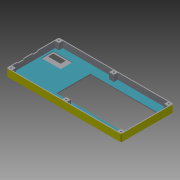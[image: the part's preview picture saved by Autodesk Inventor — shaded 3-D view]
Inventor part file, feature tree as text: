
AUTODESK INVENTOR PART (.ipt)
format: ipt  version: 2015 (Build 190159000, 159)  size: 203,776 bytes
history: native  units: mm
features: extrude x7, sketch x7, other x1, fillet x1
ambient origin geometry x8: Origin, YZ Plane, XZ Plane, XY Plane, X Axis, Y Axis, Z Axis, Center Point
bodies: Body1 (feature_tree)
feature tree (16):
  other  "ソリッド1"
  extrude  "天板"  Depth=240.0mm
  extrude  "天板くりぬき"  Depth=110.0mm
  extrude  "天板固定用ボス"  Depth=15.0mm TaperAngle=0.0deg
  extrude  "天板固定用ねじ穴"  Depth=236.0mm
  extrude  "7セグ LCD用穴"  Depth=106.0mm
  fillet  "フィレット1"  Radius=13.0mm
  extrude  "LCD用くぼみ"  Depth=8.0mm
  extrude  "Arduinoコネクタ穴"  Depth=8.0mm
  sketch  "スケッチ1"
  sketch  "スケッチ2"
  sketch  "スケッチ3"
  sketch  "スケッチ4"
  sketch  "スケッチ5"
  sketch  "スケッチ6"
  sketch  "スケッチ8"
